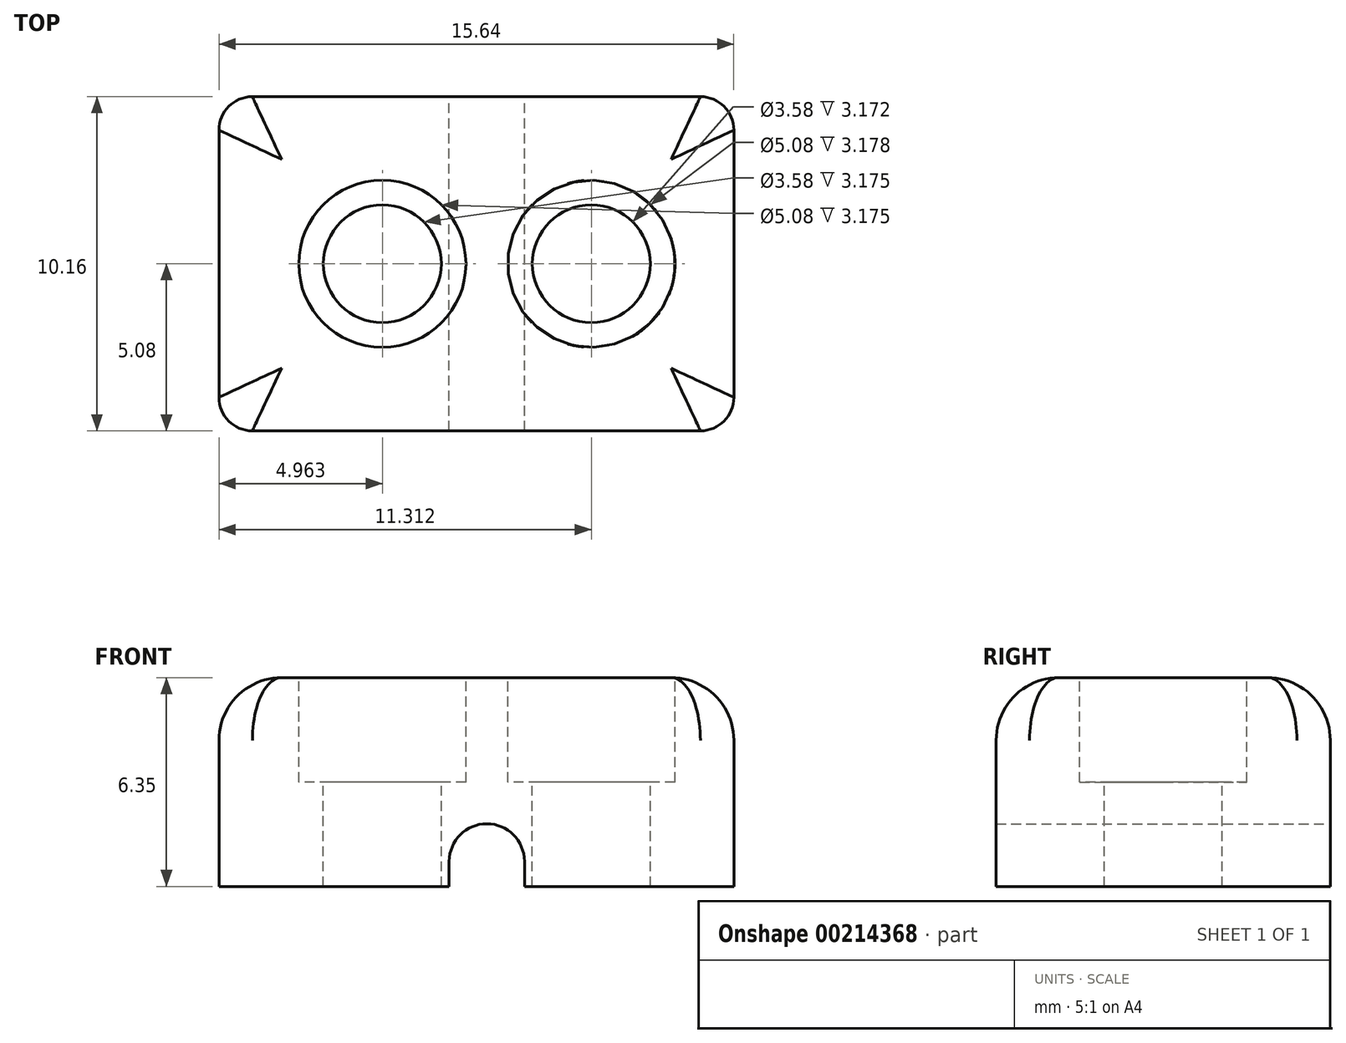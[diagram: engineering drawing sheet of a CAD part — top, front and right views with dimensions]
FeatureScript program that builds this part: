
annotation { "Feature Type Name" : "Feature", "Feature Type Description" : "" }
export const myFeature = defineFeature(function(context is Context, id is Id, definition is map)
    precondition{}
    {
        {
            var Q0;
            Q0=qCreatedBy(makeId("Top.planeOp"),FACE);
            var sketch = newSketch(context, id + "F0", { "sketchPlane" : qUnion([Q0])});
            skLineSegment(sketch, "E0.bottom", {"start": v(6.8, 5.08) * mm, "end": v(-6.8, 5.08) * mm});
            skLineSegment(sketch, "E0.top", {"start": v(6.8, -5.08) * mm, "end": v(-6.8, -5.08) * mm});
            skLineSegment(sketch, "E0.left", {"start": v(7.82, 4.06) * mm, "end": v(7.82, -4.06) * mm});
            skLineSegment(sketch, "E0.right", {"start": v(-7.82, 4.06) * mm, "end": v(-7.82, -4.06) * mm});
            skPoint(sketch, "E0.middle", {"position": v(0, 0) * mm});
            skCircle(sketch, "E1", {"center": v(3.5, 0) * mm, "radius": 1.8 * mm});
            skCircle(sketch, "E2", {"center": v(-2.86, 0) * mm, "radius": 1.8 * mm});
            skPoint(sketch, "E3.visualSharp", {"position": v(7.82, 5.08) * mm});
            skArc(sketch, "E3.filletArc", {"start": v(7.82, 4.06) * mm, "mid": v(7.53, 4.78) * mm, "end": v(6.8, 5.08) * mm});
            skPoint(sketch, "E4.visualSharp", {"position": v(7.82, -5.08) * mm});
            skArc(sketch, "E4.filletArc", {"start": v(6.8, -5.08) * mm, "mid": v(7.53, -4.78) * mm, "end": v(7.82, -4.06) * mm});
            skPoint(sketch, "E5.visualSharp", {"position": v(-7.82, -5.08) * mm});
            skArc(sketch, "E5.filletArc", {"start": v(-7.82, -4.06) * mm, "mid": v(-7.53, -4.78) * mm, "end": v(-6.8, -5.08) * mm});
            skPoint(sketch, "E6.visualSharp", {"position": v(-7.82, 5.08) * mm});
            skArc(sketch, "E6.filletArc", {"start": v(-6.8, 5.08) * mm, "mid": v(-7.53, 4.78) * mm, "end": v(-7.82, 4.06) * mm});
            skLineSegment(sketch, "E7", {"start": v(1.7, 0) * mm, "end": v(-1.07, 0) * mm, "construction": true});
            skLineSegment(sketch, "E8", {"start": v(0.32, 0) * mm, "end": v(0.32, -5.08) * mm});
            skLineSegment(sketch, "E9", {"start": v(0.32, -5.08) * mm, "end": v(0.32, 5.08) * mm, "construction": true});
            skLineSegment(sketch, "E10.0", {"start": v(1.46, -5.08) * mm, "end": v(1.46, 5.08) * mm});
            skLineSegment(sketch, "E11.0", {"start": v(-0.83, -5.08) * mm, "end": v(-0.83, 5.08) * mm});
            skSolve(sketch);
        }
        {
            var Q0;
            Q0=makeQuery(id+"F0.imprint","IMPRINT",FACE,{"disambiguationData":[TD([[makeQuery(id+"F0.imprint","IMPRINT",EDGE,{"derivedFrom":sQuery(id+"F0.wireOp",EDGE,"E0.bottom")}),1.0]])]});
            var Q1;
            Q1=makeQuery(id+"F0.imprint","IMPRINT",FACE,{"disambiguationData":[TD([[makeQuery(id+"F0.imprint","IMPRINT",EDGE,{"derivedFrom":sQuery(id+"F0.wireOp",EDGE,"E0.right")}),1.0]])]});
            var Q2;
            Q2=makeQuery(id+"F0.imprint","IMPRINT",FACE,{"disambiguationData":[TD([[makeQuery(id+"F0.imprint","IMPRINT",EDGE,{"derivedFrom":sQuery(id+"F0.wireOp",EDGE,"E0.left")}),-1.0]])]});
            var Q3;
            Q3=makeQuery(id+"F0.imprint","IMPRINT",FACE,{"disambiguationData":[TD([[makeQuery(id+"F0.imprint","IMPRINT",EDGE,{"derivedFrom":sQuery(id+"F0.wireOp",EDGE,"E1")}),1.0]])]});
            var Q4;
            Q4=makeQuery(id+"F0.imprint","IMPRINT",FACE,{"disambiguationData":[TD([[makeQuery(id+"F0.imprint","IMPRINT",EDGE,{"derivedFrom":sQuery(id+"F0.wireOp",EDGE,"E2")}),1.0]])]});
            var Q5;
            {var subQ4=sQuery(id+"F0.wireOp",EDGE,"lDdCR5JL-lnlf-xE3x-EskZ-NEjmSERAmA0B");Q5=makeQuery(id+"F0.imprint","IMPRINT",FACE,{"disambiguationData":[TD([[makeQuery(id+"F0.imprint","IMPRINT",EDGE,{"derivedFrom":subQ4}),1.0]])]});}
            var Q6;
            {var subQ4=sQuery(id+"F0.wireOp",EDGE,"lDdCR5JL-lnlf-xE3x-EskZ-NEjmSERAmA0B");Q6=makeQuery(id+"F0.imprint","IMPRINT",FACE,{"disambiguationData":[TD([[makeQuery(id+"F0.imprint","IMPRINT",EDGE,{"derivedFrom":subQ4}),-1.0]])]});}
            extrude(context, id + "F1", {"entities" : qUnion([Q0, Q1, Q2, Q3, Q4, Q5, Q6]), "depth" : 6.35 * mm});
        }
        {
            var Q0;
            {var subQ0=sQuery(id+"F0.wireOp",EDGE,"lDdCR5JL-lnlf-xE3x-EskZ-NEjmSERAmA0B");Q0=makeQuery(id+"F0.imprint","IMPRINT",FACE,{"disambiguationData":[TD([[makeQuery(id+"F0.imprint","IMPRINT",EDGE,{"derivedFrom":subQ0}),-1.0]])]});}
            var Q1;
            {var subQ0=sQuery(id+"F0.wireOp",EDGE,"lDdCR5JL-lnlf-xE3x-EskZ-NEjmSERAmA0B");Q1=makeQuery(id+"F0.imprint","IMPRINT",FACE,{"disambiguationData":[TD([[makeQuery(id+"F0.imprint","IMPRINT",EDGE,{"derivedFrom":subQ0}),1.0]])]});}
            var Q2;
            {var subQ0=sQuery(id+"F0.wireOp",EDGE,"E10.0");Q2=makeQuery(id+"F0.imprint","IMPRINT",FACE,{"disambiguationData":[TD([[makeQuery(id+"F0.imprint","IMPRINT",EDGE,{"derivedFrom":subQ0}),1.0]])]});}
            extrude(context, id + "F2", {"entities" : qUnion([Q0, Q1, Q2]), "operationType" : NewBodyOperationType.REMOVE, "depth" : 0.76 * mm});
        }
        {
            var Q0;
            Q0=makeQuery(id+"F2.boolean.opBoolean","COPY",FACE,{"derivedFrom":makeQuery(id+"F2.opExtrude","CAP_FACE",FACE,{"disambiguationData":[OSD([sQuery(id+"F0.wireOp",EDGE,"E0.bottom"),sQuery(id+"F0.wireOp",EDGE,"E0.top"),sQuery(id+"F0.wireOp",EDGE,"02de92f2-edc3-436f-bffb-b44c81d54df9.0"),sQuery(id+"F0.wireOp",EDGE,"4d53d17d-1ac7-4a13-9f7f-f51f98fd83220.MirrorCS")])],"isStart":false})});
            var sketch = newSketch(context, id + "F3", { "sketchPlane" : qUnion([Q0])});
            skLineSegment(sketch, "E12", {"start": v(0.32, 5.08) * mm, "end": v(0.32, -5.08) * mm});
            skLineSegment(sketch, "E13.0", {"start": v(-0.95, 5.08) * mm, "end": v(-0.95, -5.08) * mm});
            skSolve(sketch);
        }
        {
            var Q0;
            {var subQ0=sQuery(id+"F3.wireOp",EDGE,"E12");Q0=makeQuery(id+"F3.imprint","IMPRINT",FACE,{"disambiguationData":[TD([[makeQuery(id+"F3.imprint","IMPRINT",EDGE,{"derivedFrom":subQ0}),-1.0]])]});}
            var Q1;
            Q1=sQuery(id+"F3.wireOp",EDGE,"E12");
            revolve(context, id + "F4", {"operationType" : NewBodyOperationType.REMOVE, "entities" : qUnion([Q0]), "axis" : qUnion([Q1]), "revolveType" : RevolveType.FULL, "oppositeDirection" : true});
        }
        {
            var Q0;
            Q0=makeQuery(id+"F1.opExtrude","CAP_EDGE",EDGE,{"disambiguationData":[OSD([sQuery(id+"F0.wireOp",EDGE,"E0.top")])],"isStart":false});
            var Q1;
            Q1=makeQuery(id+"F1.opExtrude","CAP_EDGE",EDGE,{"disambiguationData":[OSD([sQuery(id+"F0.wireOp",EDGE,"E5.filletArc")])],"isStart":false});
            var Q2;
            Q2=makeQuery(id+"F1.opExtrude","CAP_EDGE",EDGE,{"disambiguationData":[OSD([sQuery(id+"F0.wireOp",EDGE,"E0.right")])],"isStart":false});
            var Q3;
            Q3=makeQuery(id+"F1.opExtrude","CAP_EDGE",EDGE,{"disambiguationData":[OSD([sQuery(id+"F0.wireOp",EDGE,"E6.filletArc")])],"isStart":false});
            var Q4;
            Q4=makeQuery(id+"F1.opExtrude","CAP_EDGE",EDGE,{"disambiguationData":[OSD([sQuery(id+"F0.wireOp",EDGE,"E0.bottom")])],"isStart":false});
            var Q5;
            Q5=makeQuery(id+"F1.opExtrude","CAP_EDGE",EDGE,{"disambiguationData":[OSD([sQuery(id+"F0.wireOp",EDGE,"E0.left")])],"isStart":false});
            var Q6;
            Q6=makeQuery(id+"F1.opExtrude","CAP_EDGE",EDGE,{"disambiguationData":[OSD([sQuery(id+"F0.wireOp",EDGE,"E4.filletArc")])],"isStart":false});
            var Q7;
            Q7=makeQuery(id+"F1.opExtrude","CAP_EDGE",EDGE,{"disambiguationData":[OSD([sQuery(id+"F0.wireOp",EDGE,"E3.filletArc")])],"isStart":false});
            fillet(context, id + "F5", {"entities" : qUnion([Q0, Q1, Q2, Q3, Q4, Q5, Q6, Q7]), "radius" : 1.9 * mm, "tangentPropagation" : true, "allowEdgeOverflow" : false});
        }
        {
            var Q0;
            Q0=makeQuery(id+"F1.opExtrude","CAP_FACE",FACE,{"disambiguationData":[OSD([sQuery(id+"F0.wireOp",EDGE,"E0.bottom"),sQuery(id+"F0.wireOp",EDGE,"E0.top"),sQuery(id+"F0.wireOp",EDGE,"E0.left"),sQuery(id+"F0.wireOp",EDGE,"E0.right"),sQuery(id+"F0.wireOp",EDGE,"E3.filletArc"),sQuery(id+"F0.wireOp",EDGE,"E4.filletArc"),sQuery(id+"F0.wireOp",EDGE,"E5.filletArc"),sQuery(id+"F0.wireOp",EDGE,"E6.filletArc")])],"isStart":false});
            var sketch = newSketch(context, id + "F6", { "sketchPlane" : qUnion([Q0])});
            skCircle(sketch, "E14", {"center": v(3.5, 0) * mm, "radius": 1.8 * mm});
            skCircle(sketch, "E15.MirrorC", {"center": v(-2.86, 0) * mm, "radius": 1.8 * mm});
            skSolve(sketch);
        }
        {
            var Q0;
            Q0=sQuery(id+"F6.wireOp",VERTEX,"E15.MirrorC.center");
            var Q1;
            Q1=sQuery(id+"F6.wireOp",VERTEX,"E14.center");
            var Q2;
            Q2=makeQuery(id+"F1.opExtrude","SWEPT_BODY",BODY,{"disambiguationData":[OSD([sQuery(id+"F0.wireOp",EDGE,"E0.bottom"),sQuery(id+"F0.wireOp",EDGE,"E0.top"),sQuery(id+"F0.wireOp",EDGE,"E0.left"),sQuery(id+"F0.wireOp",EDGE,"E0.right"),sQuery(id+"F0.wireOp",EDGE,"E3.filletArc"),sQuery(id+"F0.wireOp",EDGE,"E4.filletArc"),sQuery(id+"F0.wireOp",EDGE,"E5.filletArc"),sQuery(id+"F0.wireOp",EDGE,"E6.filletArc")])]});
            hole(context, id + "F7", {"style" : HoleStyle.C_BORE, "endStyle" : HoleEndStyle.BLIND, "holeDiameter" : 3.58 * mm, "cBoreDiameter" : 5.08 * mm, "cBoreDepth" : 3.17 * mm, "holeDepth" : 9.65 * mm, "locations" : qUnion([Q0, Q1]), "scope" : qUnion([Q2])});
        }
    });
